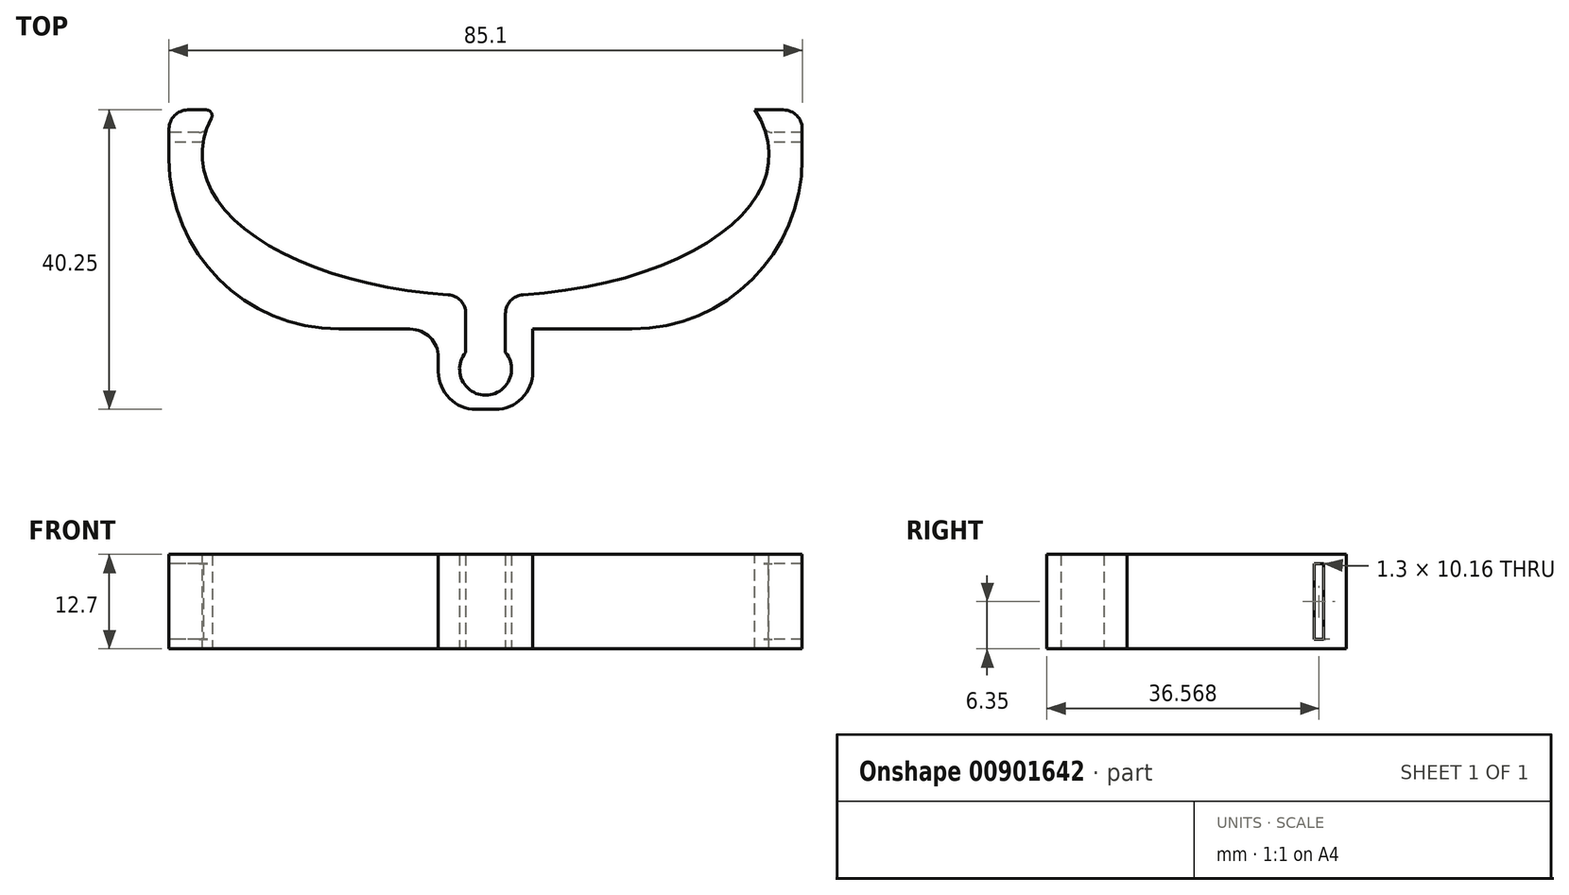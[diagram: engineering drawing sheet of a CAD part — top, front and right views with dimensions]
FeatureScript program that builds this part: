
annotation { "Feature Type Name" : "Feature", "Feature Type Description" : "" }
export const myFeature = defineFeature(function(context is Context, id is Id, definition is map)
    precondition{}
    {
        {
            var Q0;
            Q0=qCreatedBy(makeId("Top.planeOp"),FACE);
            var sketch = newSketch(context, id + "F0", { "sketchPlane" : qUnion([Q0])});
            skLineSegment(sketch, "E0.bottom", {"start": v(-42.55, 39.37) * mm, "end": v(42.55, 39.37) * mm});
            skLineSegment(sketch, "E0.top", {"start": v(-42.55, -7.62) * mm, "end": v(42.55, -7.62) * mm});
            skLineSegment(sketch, "E0.left", {"start": v(-42.55, 39.37) * mm, "end": v(-42.55, -7.62) * mm});
            skLineSegment(sketch, "E0.right", {"start": v(42.55, 39.37) * mm, "end": v(42.55, -7.62) * mm});
            skPoint(sketch, "E0.middle", {"position": v(0, 15.88) * mm});
            skSolve(sketch);
        }
        {
            var Q0;
            Q0=makeQuery(id+"F0.imprint","IMPRINT",FACE,{"disambiguationData":[TD([[makeQuery(id+"F0.imprint","IMPRINT",EDGE,{"derivedFrom":sQuery(id+"F0.wireOp",EDGE,"E0.bottom")}),-1.0]])]});
            var sketch = newSketch(context, id + "F1", { "sketchPlane" : qUnion([Q0])});
            skEllipse(sketch, "E1", {"center": v(0, 15.88) * mm, "majorRadius": 38.1 * mm, "minorRadius": 19.05 * mm, "majorAxis": v(-1, 0)});
            skSolve(sketch);
        }
        {
            var Q0;
            Q0=qCreatedBy(makeId("Top.planeOp"),FACE);
            var sketch = newSketch(context, id + "F2", { "sketchPlane" : qUnion([Q0])});
            skLineSegment(sketch, "E2.bottom", {"start": v(-6.35, -7.62) * mm, "end": v(6.35, -7.62) * mm});
            skLineSegment(sketch, "E2.top", {"start": v(-6.35, -18.41) * mm, "end": v(6.35, -18.41) * mm});
            skLineSegment(sketch, "E2.left", {"start": v(-6.35, -7.62) * mm, "end": v(-6.35, -18.41) * mm});
            skLineSegment(sketch, "E2.right", {"start": v(6.35, -7.62) * mm, "end": v(6.35, -18.41) * mm});
            skPoint(sketch, "E2.middle", {"position": v(0, -13.01) * mm});
            skSolve(sketch);
        }
        {
            var Q0;
            Q0=qCreatedBy(makeId("Top.planeOp"),FACE);
            var sketch = newSketch(context, id + "F3", { "sketchPlane" : qUnion([Q0])});
            skCircle(sketch, "E3", {"center": v(0, -13.01) * mm, "radius": 3.5 * mm});
            skSolve(sketch);
        }
        {
            var Q0;
            Q0=qCreatedBy(makeId("Top.planeOp"),FACE);
            var sketch = newSketch(context, id + "F4", { "sketchPlane" : qUnion([Q0])});
            skLineSegment(sketch, "E4.bottom", {"start": v(2.67, -0.31) * mm, "end": v(-2.67, -0.31) * mm});
            skLineSegment(sketch, "E4.top", {"start": v(2.67, -13.01) * mm, "end": v(-2.67, -13.01) * mm});
            skLineSegment(sketch, "E4.left", {"start": v(2.67, -0.31) * mm, "end": v(2.67, -13.01) * mm});
            skLineSegment(sketch, "E4.right", {"start": v(-2.67, -0.31) * mm, "end": v(-2.67, -13.01) * mm});
            skPoint(sketch, "E4.middle", {"position": v(0, -6.66) * mm});
            skSolve(sketch);
        }
        {
            var Q0;
            Q0=makeQuery(id+"F2.imprint","IMPRINT",FACE,{"disambiguationData":[TD([[makeQuery(id+"F2.imprint","IMPRINT",EDGE,{"derivedFrom":sQuery(id+"F2.wireOp",EDGE,"E2.bottom")}),-1.0]])]});
            var Q1;
            Q1=makeQuery(id+"F0.imprint","IMPRINT",FACE,{"disambiguationData":[TD([[makeQuery(id+"F0.imprint","IMPRINT",EDGE,{"derivedFrom":sQuery(id+"F0.wireOp",EDGE,"E0.bottom")}),-1.0]])]});
            extrude(context, id + "F5", {"entities" : qUnion([Q0, Q1]), "depth" : 12.7 * mm, "offsetDistance" : 25.4 * mm});
        }
        {
            var Q0;
            Q0=makeQuery(id+"F5.opExtrude","SWEPT_BODY",BODY,{"disambiguationData":[OSD([sQuery(id+"F0.wireOp",EDGE,"E0.bottom"),sQuery(id+"F0.wireOp",EDGE,"E0.top"),sQuery(id+"F0.wireOp",EDGE,"E0.left"),sQuery(id+"F0.wireOp",EDGE,"E0.right")])]});
            var Q1;
            Q1=makeQuery(id+"F5.opExtrude","SWEPT_BODY",BODY,{"disambiguationData":[OSD([sQuery(id+"F2.wireOp",EDGE,"E2.bottom"),sQuery(id+"F2.wireOp",EDGE,"E2.top"),sQuery(id+"F2.wireOp",EDGE,"E2.left"),sQuery(id+"F2.wireOp",EDGE,"E2.right")])]});
            booleanBodies(context, id + "F6", {"operationType" : BooleanOperationType.UNION, "tools" : qUnion([Q0, Q1])});
        }
        {
            var Q0;
            Q0=makeQuery(id+"F1.imprint","IMPRINT",FACE,{"disambiguationData":[TD([[makeQuery(id+"F1.imprint","IMPRINT",EDGE,{"derivedFrom":sQuery(id+"F1.wireOp",EDGE,"E1")}),1.0]])]});
            extrude(context, id + "F7", {"entities" : qUnion([Q0]), "operationType" : NewBodyOperationType.REMOVE, "depth" : 12.7 * mm, "offsetDistance" : 25.4 * mm});
        }
        {
            var Q0;
            Q0=makeQuery(id+"F3.imprint","IMPRINT",FACE,{"disambiguationData":[TD([[makeQuery(id+"F3.imprint","IMPRINT",EDGE,{"derivedFrom":sQuery(id+"F3.wireOp",EDGE,"E3")}),1.0]])]});
            var Q1;
            Q1=makeQuery(id+"F4.imprint","IMPRINT",FACE,{"disambiguationData":[TD([[makeQuery(id+"F4.imprint","IMPRINT",EDGE,{"derivedFrom":sQuery(id+"F4.wireOp",EDGE,"E4.bottom")}),1.0]])]});
            extrude(context, id + "F8", {"entities" : qUnion([Q0, Q1]), "operationType" : NewBodyOperationType.REMOVE, "depth" : 12.7 * mm, "offsetDistance" : 25.4 * mm});
        }
        {
            var Q0;
            Q0=makeQuery(id+"F6.opBoolean","MERGE",FACE,{"derivedFrom":[makeQuery(id+"F5.opExtrude","CAP_FACE",FACE,{"disambiguationData":[OSD([sQuery(id+"F0.wireOp",EDGE,"E0.bottom"),sQuery(id+"F0.wireOp",EDGE,"E0.top"),sQuery(id+"F0.wireOp",EDGE,"E0.left"),sQuery(id+"F0.wireOp",EDGE,"E0.right")])],"isStart":false}),makeQuery(id+"F5.opExtrude","CAP_FACE",FACE,{"disambiguationData":[OSD([sQuery(id+"F2.wireOp",EDGE,"E2.bottom"),sQuery(id+"F2.wireOp",EDGE,"E2.top"),sQuery(id+"F2.wireOp",EDGE,"E2.left"),sQuery(id+"F2.wireOp",EDGE,"E2.right")])],"isStart":false})]});
            var sketch = newSketch(context, id + "F9", { "sketchPlane" : qUnion([Q0])});
            skLineSegment(sketch, "E5.bottom", {"start": v(48.76, 42.5) * mm, "end": v(-49.03, 42.5) * mm});
            skLineSegment(sketch, "E5.top", {"start": v(48.76, 21.84) * mm, "end": v(-49.03, 21.84) * mm});
            skLineSegment(sketch, "E5.left", {"start": v(48.76, 42.5) * mm, "end": v(48.76, 21.84) * mm});
            skLineSegment(sketch, "E5.right", {"start": v(-49.03, 42.5) * mm, "end": v(-49.03, 21.84) * mm});
            skSolve(sketch);
        }
        {
            var Q0;
            Q0=makeQuery(id+"F9.imprint","IMPRINT",FACE,{"disambiguationData":[TD([[makeQuery(id+"F9.imprint","IMPRINT",EDGE,{"derivedFrom":sQuery(id+"F9.wireOp",EDGE,"E5.bottom")}),1.0]])]});
            var Q1;
            {var subQ1=makeQuery(id+"F5.opExtrude","CAP_EDGE",EDGE,{"disambiguationData":[OSD([sQuery(id+"F0.wireOp",EDGE,"E0.bottom")])],"isStart":false});Q1=makeQuery(id+"F9.imprint","IMPRINT",FACE,{"disambiguationData":[TD([[makeQuery(id+"F9.imprint","IMPRINT",EDGE,{"derivedFrom":subQ1}),-1.0]])]});}
            extrude(context, id + "F10", {"entities" : qUnion([Q0, Q1]), "operationType" : NewBodyOperationType.REMOVE, "oppositeDirection" : true, "depth" : 12.7 * mm, "offsetDistance" : 25.4 * mm});
        }
        {
            var Q0;
            Q0=makeQuery(id+"F8.boolean.opBoolean","INTERSECT",EDGE,{"derivedFrom":[makeQuery(id+"F7.boolean.opBoolean","COPY",FACE,{"derivedFrom":makeQuery(id+"F7.opExtrude","SWEPT_FACE",FACE,{"disambiguationData":[OSD([sQuery(id+"F1.wireOp",EDGE,"E1")])]})}),makeQuery(id+"F8.opExtrude","SWEPT_FACE",FACE,{"disambiguationData":[OSD([sQuery(id+"F4.wireOp",EDGE,"E4.left")])]})]});
            var Q1;
            Q1=makeQuery(id+"F8.boolean.opBoolean","INTERSECT",EDGE,{"derivedFrom":[makeQuery(id+"F7.boolean.opBoolean","COPY",FACE,{"derivedFrom":makeQuery(id+"F7.opExtrude","SWEPT_FACE",FACE,{"disambiguationData":[OSD([sQuery(id+"F1.wireOp",EDGE,"E1")])]})}),makeQuery(id+"F8.opExtrude","SWEPT_FACE",FACE,{"disambiguationData":[OSD([sQuery(id+"F4.wireOp",EDGE,"E4.right")])]})]});
            fillet(context, id + "F11", {"entities" : qUnion([Q0, Q1]), "radius" : 2.54 * mm, "tangentPropagation" : true, "allowEdgeOverflow" : false});
        }
        {
            var Q0;
            Q0=makeQuery(id+"F5.opExtrude","SWEPT_EDGE",EDGE,{"disambiguationData":[OSD([sQuery(id+"F2.wireOp",EDGE,"E2.bottom"),sQuery(id+"F2.wireOp",EDGE,"E2.left")])]});
            var Q1;
            Q1=makeQuery(id+"F5.opExtrude","SWEPT_EDGE",EDGE,{"disambiguationData":[OSD([sQuery(id+"F2.wireOp",EDGE,"E2.bottom"),sQuery(id+"F2.wireOp",EDGE,"E2.right")])]});
            fillet(context, id + "F12", {"entities" : qUnion([Q0, Q1]), "radius" : 3.8 * mm, "tangentPropagation" : true, "allowEdgeOverflow" : false});
        }
        {
            var Q0;
            Q0=makeQuery(id+"F5.opExtrude","SWEPT_EDGE",EDGE,{"disambiguationData":[OSD([sQuery(id+"F0.wireOp",EDGE,"E0.top"),sQuery(id+"F0.wireOp",EDGE,"E0.left")])]});
            var Q1;
            Q1=makeQuery(id+"F5.opExtrude","SWEPT_EDGE",EDGE,{"disambiguationData":[OSD([sQuery(id+"F0.wireOp",EDGE,"E0.top"),sQuery(id+"F0.wireOp",EDGE,"E0.right")])]});
            fillet(context, id + "F13", {"entities" : qUnion([Q0, Q1]), "radius" : 22.86 * mm, "tangentPropagation" : true, "allowEdgeOverflow" : false});
        }
        {
            var Q0;
            Q0=makeQuery(id+"F5.opExtrude","SWEPT_EDGE",EDGE,{"disambiguationData":[OSD([sQuery(id+"F2.wireOp",EDGE,"E2.top"),sQuery(id+"F2.wireOp",EDGE,"E2.left")])]});
            var Q1;
            Q1=makeQuery(id+"F5.opExtrude","SWEPT_EDGE",EDGE,{"disambiguationData":[OSD([sQuery(id+"F2.wireOp",EDGE,"E2.top"),sQuery(id+"F2.wireOp",EDGE,"E2.right")])]});
            fillet(context, id + "F14", {"entities" : qUnion([Q0, Q1]), "radius" : 5.08 * mm, "tangentPropagation" : true, "allowEdgeOverflow" : false});
        }
        {
            var Q0;
            {var subQ0=sQuery(id+"F9.wireOp",EDGE,"E5.top");var subQ1=sQuery(id+"F0.wireOp",EDGE,"E0.left");var subQ2=makeQuery(id+"F9.imprint","INTERSECT",VERTEX,{"derivedFrom":[makeQuery(id+"F5.opExtrude","CAP_EDGE",EDGE,{"disambiguationData":[OSD([subQ1])],"isStart":false}),subQ0]});Q0=makeQuery(id+"F10.boolean.opBoolean","INTERSECT",EDGE,{"derivedFrom":[makeQuery(id+"F5.opExtrude","SWEPT_FACE",FACE,{"disambiguationData":[OSD([subQ1])]}),makeQuery(id+"F10.opExtrude","SWEPT_FACE",FACE,{"disambiguationData":[OSD([subQ0]),TDD([makeQuery(id+"F9.imprint","IMPRINT",EDGE,{"disambiguationData":[TD([[subQ2,1.0]])],"derivedFrom":subQ0}),makeQuery(id+"F9.imprint","IMPRINT",EDGE,{"disambiguationData":[TD([[makeQuery(id+"F9.imprint","INTERSECT",VERTEX,{"derivedFrom":[subQ0,sQuery(id+"F9.wireOp",EDGE,"E5.right")]}),1.0]])],"derivedFrom":subQ0})])]})]});}
            var Q1;
            {var subQ0=sQuery(id+"F9.wireOp",EDGE,"E5.top");var subQ1=sQuery(id+"F0.wireOp",EDGE,"E0.right");var subQ2=makeQuery(id+"F9.imprint","INTERSECT",VERTEX,{"derivedFrom":[makeQuery(id+"F5.opExtrude","CAP_EDGE",EDGE,{"disambiguationData":[OSD([subQ1])],"isStart":false}),subQ0]});Q1=makeQuery(id+"F10.boolean.opBoolean","INTERSECT",EDGE,{"derivedFrom":[makeQuery(id+"F5.opExtrude","SWEPT_FACE",FACE,{"disambiguationData":[OSD([subQ1])]}),makeQuery(id+"F10.opExtrude","SWEPT_FACE",FACE,{"disambiguationData":[OSD([subQ0]),TDD([makeQuery(id+"F9.imprint","IMPRINT",EDGE,{"disambiguationData":[TD([[makeQuery(id+"F9.imprint","INTERSECT",VERTEX,{"derivedFrom":[subQ0,sQuery(id+"F9.wireOp",EDGE,"E5.left")]}),-1.0]])],"derivedFrom":subQ0}),makeQuery(id+"F9.imprint","IMPRINT",EDGE,{"disambiguationData":[TD([[subQ2,-1.0]])],"derivedFrom":subQ0})])]})]});}
            fillet(context, id + "F15", {"entities" : qUnion([Q0, Q1]), "radius" : 2.54 * mm, "tangentPropagation" : true, "allowEdgeOverflow" : false});
        }
        {
            var Q0;
            {var subQ0=sQuery(id+"F9.wireOp",EDGE,"E5.top");var subQ1=sQuery(id+"F1.wireOp",EDGE,"E1");Q0=makeQuery(id+"F10.boolean.opBoolean","COPY",EDGE,{"derivedFrom":makeQuery(id+"F10.opExtrude","SWEPT_EDGE",EDGE,{"disambiguationData":[OSD([subQ1,subQ0]),TDD([makeQuery(id+"F9.imprint","INTERSECT",VERTEX,{"disambiguationData":[OD(1.0)],"derivedFrom":[makeQuery(id+"F7.boolean.opBoolean","COPY",EDGE,{"derivedFrom":makeQuery(id+"F7.opExtrude","CAP_EDGE",EDGE,{"disambiguationData":[OSD([subQ1])],"isStart":false})}),subQ0]})])]})});}
            var Q1;
            {var subQ0=sQuery(id+"F9.wireOp",EDGE,"E5.top");var subQ1=sQuery(id+"F1.wireOp",EDGE,"E1");Q1=makeQuery(id+"F10.boolean.opBoolean","COPY",EDGE,{"derivedFrom":makeQuery(id+"F10.opExtrude","SWEPT_EDGE",EDGE,{"disambiguationData":[OSD([subQ1,subQ0]),TDD([makeQuery(id+"F9.imprint","INTERSECT",VERTEX,{"disambiguationData":[OD(0.0)],"derivedFrom":[makeQuery(id+"F7.boolean.opBoolean","COPY",EDGE,{"derivedFrom":makeQuery(id+"F7.opExtrude","CAP_EDGE",EDGE,{"disambiguationData":[OSD([subQ1])],"isStart":false})}),subQ0]})])]})});}
            fillet(context, id + "F16", {"entities" : qUnion([Q0, Q1]), "radius" : 0.76 * mm, "tangentPropagation" : true, "allowEdgeOverflow" : false});
        }
        {
            var Q0;
            Q0=makeQuery(id+"F5.opExtrude","SWEPT_FACE",FACE,{"disambiguationData":[OSD([sQuery(id+"F0.wireOp",EDGE,"E0.left")])]});
            var sketch = newSketch(context, id + "F17", { "sketchPlane" : qUnion([Q0])});
            skLineSegment(sketch, "E6.bottom", {"start": v(-17.5, 11.43) * mm, "end": v(-18.8, 11.43) * mm});
            skLineSegment(sketch, "E6.top", {"start": v(-17.5, 1.27) * mm, "end": v(-18.8, 1.27) * mm});
            skLineSegment(sketch, "E6.left", {"start": v(-17.5, 11.43) * mm, "end": v(-17.5, 1.27) * mm});
            skLineSegment(sketch, "E6.right", {"start": v(-18.8, 11.43) * mm, "end": v(-18.8, 1.27) * mm});
            skPoint(sketch, "E6.middle", {"position": v(-18.16, 6.35) * mm});
            skPoint(sketch, "E7", {"position": v(-19.3, 6.35) * mm});
            skSolve(sketch);
        }
        {
            var Q0;
            Q0=makeQuery(id+"F17.imprint","IMPRINT",FACE,{"disambiguationData":[TD([[makeQuery(id+"F17.imprint","IMPRINT",EDGE,{"derivedFrom":sQuery(id+"F17.wireOp",EDGE,"E6.bottom")}),1.0]])]});
            extrude(context, id + "F18", {"entities" : qUnion([Q0]), "operationType" : NewBodyOperationType.REMOVE, "oppositeDirection" : true, "depth" : 88.9 * mm, "offsetDistance" : 25.4 * mm});
        }
        {
            var Q0;
            {var subQ10=sQuery(id+"F1.wireOp",EDGE,"E1");Q0=makeQuery(id+"F18.boolean.opBoolean","INTERSECT",EDGE,{"derivedFrom":[makeQuery(id+"F10.boolean.opBoolean","SPLIT",FACE,{"disambiguationData":[TD([makeQuery(id+"F8.boolean.opBoolean","COPY",FACE,{"derivedFrom":makeQuery(id+"F8.opExtrude","SWEPT_FACE",FACE,{"disambiguationData":[OSD([sQuery(id+"F4.wireOp",EDGE,"E4.left")])]})})])],"derivedFrom":makeQuery(id+"F7.boolean.opBoolean","COPY",FACE,{"derivedFrom":makeQuery(id+"F7.opExtrude","SWEPT_FACE",FACE,{"disambiguationData":[OSD([subQ10])]})})}),makeQuery(id+"F18.opExtrude","SWEPT_FACE",FACE,{"disambiguationData":[OSD([sQuery(id+"F17.wireOp",EDGE,"E6.right")])]})]});}
            var Q1;
            {var subQ10=sQuery(id+"F1.wireOp",EDGE,"E1");Q1=makeQuery(id+"F18.boolean.opBoolean","INTERSECT",EDGE,{"derivedFrom":[makeQuery(id+"F10.boolean.opBoolean","SPLIT",FACE,{"disambiguationData":[TD([makeQuery(id+"F8.boolean.opBoolean","COPY",FACE,{"derivedFrom":makeQuery(id+"F8.opExtrude","SWEPT_FACE",FACE,{"disambiguationData":[OSD([sQuery(id+"F4.wireOp",EDGE,"E4.right")])]})})])],"derivedFrom":makeQuery(id+"F7.boolean.opBoolean","COPY",FACE,{"derivedFrom":makeQuery(id+"F7.opExtrude","SWEPT_FACE",FACE,{"disambiguationData":[OSD([subQ10])]})})}),makeQuery(id+"F18.opExtrude","SWEPT_FACE",FACE,{"disambiguationData":[OSD([sQuery(id+"F17.wireOp",EDGE,"E6.right")])]})]});}
            fillet(context, id + "F19", {"entities" : qUnion([Q0, Q1]), "radius" : 1.27 * mm, "tangentPropagation" : true, "allowEdgeOverflow" : false});
        }
    });
